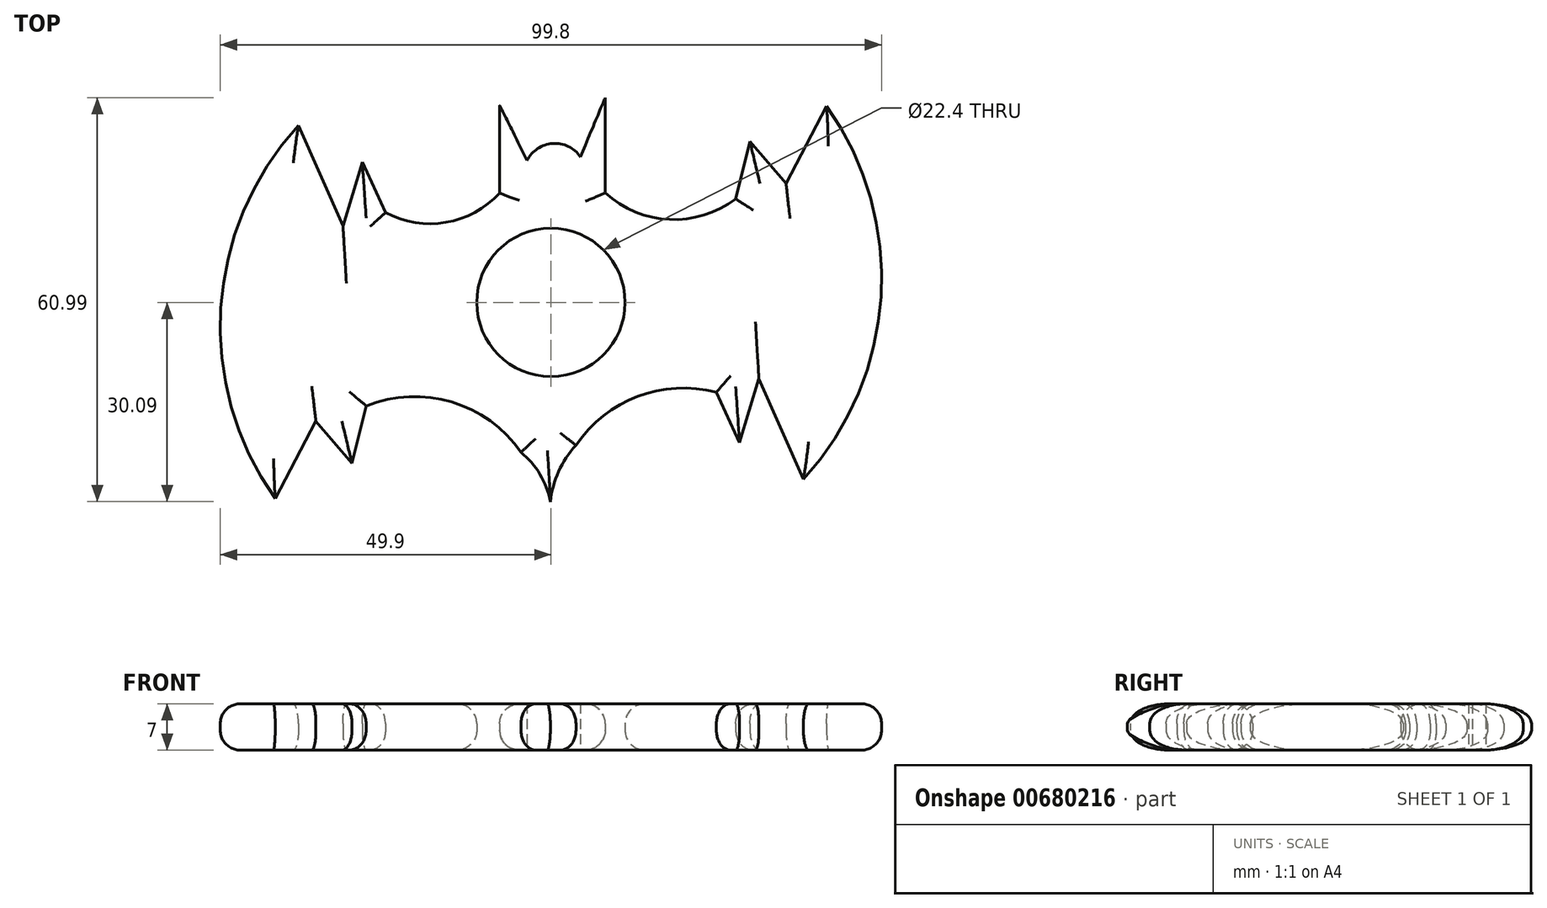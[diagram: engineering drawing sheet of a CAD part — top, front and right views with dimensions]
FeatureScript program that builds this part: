
annotation { "Feature Type Name" : "Feature", "Feature Type Description" : "" }
export const myFeature = defineFeature(function(context is Context, id is Id, definition is map)
    precondition{}
    {
        {
            var Q0;
            Q0=qCreatedBy(makeId("Top.planeOp"),FACE);
            var sketch = newSketch(context, id + "F0", { "sketchPlane" : qUnion([Q0])});
            skCircle(sketch, "E0", {"center": v(0, 0) * mm, "radius": 11.2 * mm});
            skCircle(sketch, "E1", {"center": v(0, 0) * mm, "radius": 13.2 * mm});
            skArc(sketch, "E2", {"start": v(-38.1, 26.72) * mm, "mid": v(-49.82, -0.84) * mm, "end": v(-41.61, -29.64) * mm});
            skArc(sketch, "E3.1.0", {"start": v(38.1, -26.72) * mm, "mid": v(49.82, 0.84) * mm, "end": v(41.61, 29.64) * mm});
            skLineSegment(sketch, "E4", {"start": v(-41.61, -29.64) * mm, "end": v(-35.48, -17.96) * mm});
            skLineSegment(sketch, "E5", {"start": v(-35.48, -17.96) * mm, "end": v(-35.48, -24.97) * mm});
            skArc(sketch, "E6", {"start": v(-4.53, -22.63) * mm, "mid": v(-14.98, -15.03) * mm, "end": v(-27.89, -15.62) * mm});
            skLineSegment(sketch, "E7.1.0", {"start": v(41.61, 29.64) * mm, "end": v(35.48, 17.96) * mm});
            skLineSegment(sketch, "E7.1.1", {"start": v(35.48, 17.96) * mm, "end": v(30.03, 24.29) * mm});
            skLineSegment(sketch, "E7.1.2", {"start": v(30.03, 24.29) * mm, "end": v(27.89, 15.62) * mm});
            skLineSegment(sketch, "E8", {"start": v(38.1, -26.72) * mm, "end": v(31.4, -11.53) * mm});
            skLineSegment(sketch, "E9", {"start": v(31.4, -11.53) * mm, "end": v(28.47, -21.17) * mm});
            skLineSegment(sketch, "E10", {"start": v(28.47, -21.17) * mm, "end": v(24.97, -13.58) * mm});
            skArc(sketch, "E11.1.0", {"start": v(-24.97, 13.58) * mm, "mid": v(-15.85, 12.08) * mm, "end": v(-7.74, 16.5) * mm});
            skLineSegment(sketch, "E11.1.2", {"start": v(-28.47, 21.17) * mm, "end": v(-24.97, 13.58) * mm});
            skLineSegment(sketch, "E11.1.4", {"start": v(-31.4, 11.53) * mm, "end": v(-28.47, 21.17) * mm});
            skLineSegment(sketch, "E11.1.5", {"start": v(-38.1, 26.72) * mm, "end": v(-31.4, 11.53) * mm});
            skArc(sketch, "E12", {"start": v(0, -34.06) * mm, "mid": v(-0.76, -27.75) * mm, "end": v(-4.53, -22.63) * mm});
            skArc(sketch, "E13.1.0", {"start": v(8.2, 16.53) * mm, "mid": v(17.88, 12.52) * mm, "end": v(27.89, 15.62) * mm});
            skLineSegment(sketch, "E14", {"start": v(-7.74, 16.5) * mm, "end": v(-7.74, 29.75) * mm});
            skLineSegment(sketch, "E15", {"start": v(-7.74, 29.75) * mm, "end": v(-3.6, 21.41) * mm});
            skLineSegment(sketch, "E16", {"start": v(8.2, 16.53) * mm, "end": v(8.2, 30.9) * mm});
            skLineSegment(sketch, "E17", {"start": v(8.2, 30.9) * mm, "end": v(4.45, 21.97) * mm});
            skArc(sketch, "E18", {"start": v(4.45, 21.97) * mm, "mid": v(0.27, 24) * mm, "end": v(-3.6, 21.41) * mm});
            skArc(sketch, "E19", {"start": v(24.97, -13.58) * mm, "mid": v(13.1, -14.2) * mm, "end": v(3.78, -21.57) * mm});
            skArc(sketch, "E20", {"start": v(3.78, -21.57) * mm, "mid": v(0.47, -27.38) * mm, "end": v(0, -34.06) * mm});
            skLineSegment(sketch, "E21.1.0", {"start": v(-35.48, -17.96) * mm, "end": v(-30.03, -24.29) * mm});
            skLineSegment(sketch, "E21.1.1", {"start": v(-30.03, -24.29) * mm, "end": v(-27.89, -15.62) * mm});
            skSolve(sketch);
        }
        {
            var Q0;
            Q0=makeQuery(id+"F0.imprint","IMPRINT",FACE,{"disambiguationData":[TD([[makeQuery(id+"F0.imprint","IMPRINT",EDGE,{"derivedFrom":sQuery(id+"F0.wireOp",EDGE,"E0")}),-1.0]])]});
            var Q1;
            Q1=makeQuery(id+"F0.imprint","IMPRINT",FACE,{"disambiguationData":[TD([[makeQuery(id+"F0.imprint","IMPRINT",EDGE,{"derivedFrom":sQuery(id+"F0.wireOp",EDGE,"E1")}),-1.0]])]});
            extrude(context, id + "F1", {"entities" : qUnion([Q0, Q1]), "depth" : 7 * mm, "offsetDistance" : 25 * mm});
        }
        {
            var Q0;
            Q0=makeQuery(id+"F1.opExtrude","CAP_EDGE",EDGE,{"disambiguationData":[OSD([sQuery(id+"F0.wireOp",EDGE,"E20")])],"isStart":false});
            var Q1;
            Q1=makeQuery(id+"F1.opExtrude","CAP_EDGE",EDGE,{"disambiguationData":[OSD([sQuery(id+"F0.wireOp",EDGE,"E19")])],"isStart":false});
            var Q2;
            Q2=makeQuery(id+"F1.opExtrude","CAP_EDGE",EDGE,{"disambiguationData":[OSD([sQuery(id+"F0.wireOp",EDGE,"E9")])],"isStart":false});
            var Q3;
            Q3=makeQuery(id+"F1.opExtrude","CAP_EDGE",EDGE,{"disambiguationData":[OSD([sQuery(id+"F0.wireOp",EDGE,"E3.1.0")])],"isStart":false});
            var Q4;
            Q4=makeQuery(id+"F1.opExtrude","CAP_EDGE",EDGE,{"disambiguationData":[OSD([sQuery(id+"F0.wireOp",EDGE,"E8")])],"isStart":false});
            var Q5;
            Q5=makeQuery(id+"F1.opExtrude","CAP_EDGE",EDGE,{"disambiguationData":[OSD([sQuery(id+"F0.wireOp",EDGE,"E7.1.0")])],"isStart":false});
            var Q6;
            Q6=makeQuery(id+"F1.opExtrude","CAP_EDGE",EDGE,{"disambiguationData":[OSD([sQuery(id+"F0.wireOp",EDGE,"E7.1.1")])],"isStart":false});
            var Q7;
            Q7=makeQuery(id+"F1.opExtrude","CAP_EDGE",EDGE,{"disambiguationData":[OSD([sQuery(id+"F0.wireOp",EDGE,"E7.1.2")])],"isStart":false});
            var Q8;
            Q8=makeQuery(id+"F1.opExtrude","CAP_EDGE",EDGE,{"disambiguationData":[OSD([sQuery(id+"F0.wireOp",EDGE,"E13.1.0")])],"isStart":false});
            var Q9;
            Q9=makeQuery(id+"F1.opExtrude","CAP_EDGE",EDGE,{"disambiguationData":[OSD([sQuery(id+"F0.wireOp",EDGE,"E16")])],"isStart":false});
            var Q10;
            Q10=makeQuery(id+"F1.opExtrude","CAP_EDGE",EDGE,{"disambiguationData":[OSD([sQuery(id+"F0.wireOp",EDGE,"E14")])],"isStart":false});
            var Q11;
            Q11=makeQuery(id+"F1.opExtrude","CAP_EDGE",EDGE,{"disambiguationData":[OSD([sQuery(id+"F0.wireOp",EDGE,"E11.1.0")])],"isStart":false});
            var Q12;
            Q12=makeQuery(id+"F1.opExtrude","CAP_EDGE",EDGE,{"disambiguationData":[OSD([sQuery(id+"F0.wireOp",EDGE,"E11.1.2")])],"isStart":false});
            var Q13;
            Q13=makeQuery(id+"F1.opExtrude","CAP_EDGE",EDGE,{"disambiguationData":[OSD([sQuery(id+"F0.wireOp",EDGE,"E11.1.5")])],"isStart":false});
            var Q14;
            Q14=makeQuery(id+"F1.opExtrude","CAP_EDGE",EDGE,{"disambiguationData":[OSD([sQuery(id+"F0.wireOp",EDGE,"E11.1.4")])],"isStart":false});
            var Q15;
            Q15=makeQuery(id+"F1.opExtrude","CAP_EDGE",EDGE,{"disambiguationData":[OSD([sQuery(id+"F0.wireOp",EDGE,"E2")])],"isStart":false});
            var Q16;
            Q16=makeQuery(id+"F1.opExtrude","CAP_EDGE",EDGE,{"disambiguationData":[OSD([sQuery(id+"F0.wireOp",EDGE,"E4")])],"isStart":false});
            var Q17;
            Q17=makeQuery(id+"F1.opExtrude","CAP_EDGE",EDGE,{"disambiguationData":[OSD([sQuery(id+"F0.wireOp",EDGE,"wEF84jsq-XExs-cQrN-D3yr-Ib7uIkRzdJAm")])],"isStart":false});
            var Q18;
            Q18=makeQuery(id+"F1.opExtrude","CAP_EDGE",EDGE,{"disambiguationData":[OSD([sQuery(id+"F0.wireOp",EDGE,"E12")])],"isStart":false});
            var Q19;
            Q19=makeQuery(id+"F1.opExtrude","CAP_EDGE",EDGE,{"disambiguationData":[OSD([sQuery(id+"F0.wireOp",EDGE,"E5")])],"isStart":false});
            var Q20;
            Q20=makeQuery(id+"F1.opExtrude","CAP_EDGE",EDGE,{"disambiguationData":[OSD([sQuery(id+"F0.wireOp",EDGE,"E10")])],"isStart":false});
            var Q21;
            Q21=makeQuery(id+"F1.opExtrude","CAP_EDGE",EDGE,{"disambiguationData":[OSD([sQuery(id+"F0.wireOp",EDGE,"E21.1.1")])],"isStart":false});
            var Q22;
            Q22=makeQuery(id+"F1.opExtrude","CAP_EDGE",EDGE,{"disambiguationData":[OSD([sQuery(id+"F0.wireOp",EDGE,"E6")])],"isStart":false});
            var Q23;
            Q23=makeQuery(id+"F1.opExtrude","CAP_EDGE",EDGE,{"disambiguationData":[OSD([sQuery(id+"F0.wireOp",EDGE,"E21.1.0")])],"isStart":false});
            var Q24;
            Q24=makeQuery(id+"F1.opExtrude","CAP_EDGE",EDGE,{"disambiguationData":[OSD([sQuery(id+"F0.wireOp",EDGE,"E3.1.0")])],"isStart":true});
            var Q25;
            Q25=makeQuery(id+"F1.opExtrude","CAP_EDGE",EDGE,{"disambiguationData":[OSD([sQuery(id+"F0.wireOp",EDGE,"E8")])],"isStart":true});
            var Q26;
            Q26=makeQuery(id+"F1.opExtrude","CAP_EDGE",EDGE,{"disambiguationData":[OSD([sQuery(id+"F0.wireOp",EDGE,"E9")])],"isStart":true});
            var Q27;
            Q27=makeQuery(id+"F1.opExtrude","CAP_EDGE",EDGE,{"disambiguationData":[OSD([sQuery(id+"F0.wireOp",EDGE,"E10")])],"isStart":true});
            var Q28;
            Q28=makeQuery(id+"F1.opExtrude","CAP_EDGE",EDGE,{"disambiguationData":[OSD([sQuery(id+"F0.wireOp",EDGE,"E19")])],"isStart":true});
            var Q29;
            Q29=makeQuery(id+"F1.opExtrude","CAP_EDGE",EDGE,{"disambiguationData":[OSD([sQuery(id+"F0.wireOp",EDGE,"E6")])],"isStart":true});
            var Q30;
            Q30=makeQuery(id+"F1.opExtrude","CAP_EDGE",EDGE,{"disambiguationData":[OSD([sQuery(id+"F0.wireOp",EDGE,"E12")])],"isStart":true});
            var Q31;
            Q31=makeQuery(id+"F1.opExtrude","CAP_EDGE",EDGE,{"disambiguationData":[OSD([sQuery(id+"F0.wireOp",EDGE,"E20")])],"isStart":true});
            var Q32;
            Q32=makeQuery(id+"F1.opExtrude","CAP_EDGE",EDGE,{"disambiguationData":[OSD([sQuery(id+"F0.wireOp",EDGE,"E21.1.1")])],"isStart":true});
            var Q33;
            Q33=makeQuery(id+"F1.opExtrude","CAP_EDGE",EDGE,{"disambiguationData":[OSD([sQuery(id+"F0.wireOp",EDGE,"E21.1.0")])],"isStart":true});
            var Q34;
            Q34=makeQuery(id+"F1.opExtrude","CAP_EDGE",EDGE,{"disambiguationData":[OSD([sQuery(id+"F0.wireOp",EDGE,"E4")])],"isStart":true});
            var Q35;
            Q35=makeQuery(id+"F1.opExtrude","CAP_EDGE",EDGE,{"disambiguationData":[OSD([sQuery(id+"F0.wireOp",EDGE,"E2")])],"isStart":true});
            var Q36;
            Q36=makeQuery(id+"F1.opExtrude","CAP_EDGE",EDGE,{"disambiguationData":[OSD([sQuery(id+"F0.wireOp",EDGE,"E11.1.5")])],"isStart":true});
            var Q37;
            Q37=makeQuery(id+"F1.opExtrude","CAP_EDGE",EDGE,{"disambiguationData":[OSD([sQuery(id+"F0.wireOp",EDGE,"E11.1.4")])],"isStart":true});
            var Q38;
            Q38=makeQuery(id+"F1.opExtrude","CAP_EDGE",EDGE,{"disambiguationData":[OSD([sQuery(id+"F0.wireOp",EDGE,"E14")])],"isStart":true});
            var Q39;
            Q39=makeQuery(id+"F1.opExtrude","CAP_EDGE",EDGE,{"disambiguationData":[OSD([sQuery(id+"F0.wireOp",EDGE,"E16")])],"isStart":true});
            var Q40;
            Q40=makeQuery(id+"F1.opExtrude","CAP_EDGE",EDGE,{"disambiguationData":[OSD([sQuery(id+"F0.wireOp",EDGE,"E13.1.0")])],"isStart":true});
            var Q41;
            Q41=makeQuery(id+"F1.opExtrude","CAP_EDGE",EDGE,{"disambiguationData":[OSD([sQuery(id+"F0.wireOp",EDGE,"E7.1.2")])],"isStart":true});
            var Q42;
            Q42=makeQuery(id+"F1.opExtrude","CAP_EDGE",EDGE,{"disambiguationData":[OSD([sQuery(id+"F0.wireOp",EDGE,"E7.1.1")])],"isStart":true});
            var Q43;
            Q43=makeQuery(id+"F1.opExtrude","CAP_EDGE",EDGE,{"disambiguationData":[OSD([sQuery(id+"F0.wireOp",EDGE,"E7.1.0")])],"isStart":true});
            var Q44;
            Q44=makeQuery(id+"F1.opExtrude","CAP_EDGE",EDGE,{"disambiguationData":[OSD([sQuery(id+"F0.wireOp",EDGE,"E11.1.0")])],"isStart":true});
            var Q45;
            Q45=makeQuery(id+"F1.opExtrude","CAP_EDGE",EDGE,{"disambiguationData":[OSD([sQuery(id+"F0.wireOp",EDGE,"E11.1.2")])],"isStart":true});
            fillet(context, id + "F2", {"entities" : qUnion([Q0, Q1, Q2, Q3, Q4, Q5, Q6, Q7, Q8, Q9, Q10, Q11, Q12, Q13, Q14, Q15, Q16, Q17, Q18, Q19, Q20, Q21, Q22, Q23, Q24, Q25, Q26, Q27, Q28, Q29, Q30, Q31, Q32, Q33, Q34, Q35, Q36, Q37, Q38, Q39, Q40, Q41, Q42, Q43, Q44, Q45]), "radius" : 3 * mm, "tangentPropagation" : true, "allowEdgeOverflow" : false});
        }
        {
            var Q0;
            Q0=makeQuery(id+"F1.opExtrude","CAP_EDGE",EDGE,{"disambiguationData":[OSD([sQuery(id+"F0.wireOp",EDGE,"E0")])],"isStart":true});
            var Q1;
            Q1=makeQuery(id+"F1.opExtrude","CAP_EDGE",EDGE,{"disambiguationData":[OSD([sQuery(id+"F0.wireOp",EDGE,"E0")])],"isStart":false});
            fillet(context, id + "F3", {"entities" : qUnion([Q0, Q1]), "radius" : 3 * mm, "tangentPropagation" : true, "allowEdgeOverflow" : false});
        }
    });
